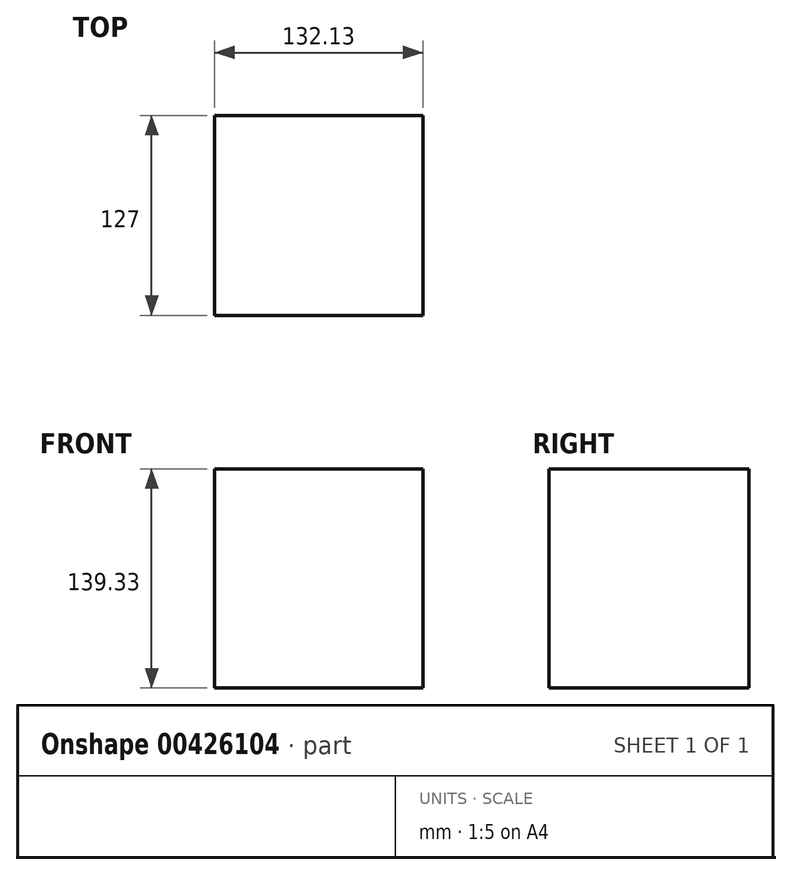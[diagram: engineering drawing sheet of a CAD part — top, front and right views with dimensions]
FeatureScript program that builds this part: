
annotation { "Feature Type Name" : "Feature", "Feature Type Description" : "" }
export const myFeature = defineFeature(function(context is Context, id is Id, definition is map)
    precondition{}
    {
        {
            var Q0;
            Q0=qCreatedBy(makeId("Front.planeOp"),FACE);
            var sketch = newSketch(context, id + "F0", { "sketchPlane" : qUnion([Q0])});
            skLineSegment(sketch, "E0.bottom", {"start": v(-123.6, 69.75) * mm, "end": v(8.53, 69.75) * mm});
            skLineSegment(sketch, "E0.top", {"start": v(-123.6, -69.58) * mm, "end": v(8.53, -69.58) * mm});
            skLineSegment(sketch, "E0.left", {"start": v(-123.6, 69.75) * mm, "end": v(-123.6, -69.58) * mm});
            skLineSegment(sketch, "E0.right", {"start": v(8.53, 69.75) * mm, "end": v(8.53, -69.58) * mm});
            skSolve(sketch);
        }
        {
            var Q0;
            Q0=makeQuery(id+"F0.imprint","IMPRINT",FACE,{"disambiguationData":[TD([[makeQuery(id+"F0.imprint","IMPRINT",EDGE,{"derivedFrom":sQuery(id+"F0.wireOp",EDGE,"E0.bottom")}),-1.0]])]});
            extrude(context, id + "F1", {"entities" : qUnion([Q0]), "depth" : 127 * mm, "offsetDistance" : 25.4 * mm});
        }
    });
